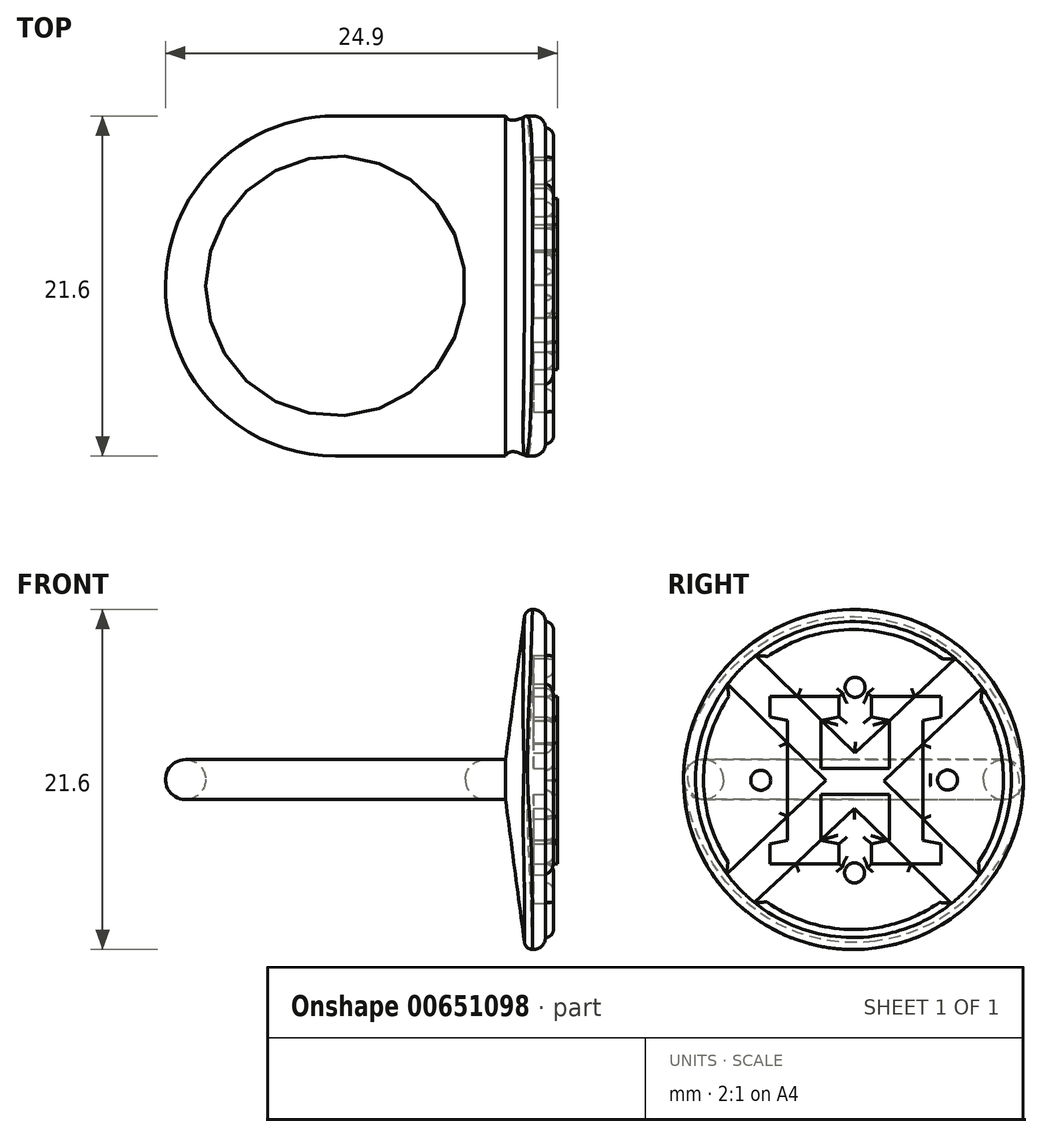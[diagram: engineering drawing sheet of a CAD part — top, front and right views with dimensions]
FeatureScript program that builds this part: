
annotation { "Feature Type Name" : "Feature", "Feature Type Description" : "" }
export const myFeature = defineFeature(function(context is Context, id is Id, definition is map)
    precondition{}
    {
        {
            var Q0;
            Q0=qCreatedBy(makeId("Top.planeOp"),FACE);
            var sketch = newSketch(context, id + "F0", { "sketchPlane" : qUnion([Q0])});
            skCircle(sketch, "E0", {"center": v(0, 0) * mm, "radius": 8.26 * mm});
            skCircle(sketch, "E1.0", {"center": v(0, 0) * mm, "radius": 10.8 * mm});
            skLineSegment(sketch, "E2", {"start": v(0, -10.8) * mm, "end": v(28.84, -10.8) * mm});
            skLineSegment(sketch, "E3", {"start": v(0, 10.8) * mm, "end": v(27.85, 10.8) * mm});
            skLineSegment(sketch, "E4", {"start": v(10.8, 0) * mm, "end": v(10.8, 10.8) * mm});
            skLineSegment(sketch, "E5", {"start": v(10.8, 10.8) * mm, "end": v(10.8, -10.8) * mm});
            skSolve(sketch);
        }
        {
            var Q0;
            Q0=qSketchRegion(id+"F0",true);
            extrude(context, id + "F1", {"entities" : qUnion([Q0]), "depth" : 2.54 * mm, "offsetDistance" : 25.4 * mm});
        }
        {
            var Q0;
            Q0=makeQuery(id+"F1.opExtrude","CAP_EDGE",EDGE,{"disambiguationData":[OSD([sQuery(id+"F0.wireOp",EDGE,"E0")])],"isStart":false});
            var Q1;
            Q1=makeQuery(id+"F1.opExtrude","CAP_EDGE",EDGE,{"disambiguationData":[OSD([sQuery(id+"F0.wireOp",EDGE,"E0")])],"isStart":true});
            var Q2;
            Q2=makeQuery(id+"F1.opExtrude","CAP_EDGE",EDGE,{"disambiguationData":[OSD([sQuery(id+"F0.wireOp",EDGE,"E1.0")])],"isStart":false});
            var Q3;
            Q3=makeQuery(id+"F1.opExtrude","CAP_EDGE",EDGE,{"disambiguationData":[OSD([sQuery(id+"F0.wireOp",EDGE,"E1.0")])],"isStart":true});
            fillet(context, id + "F2", {"entities" : qUnion([Q0, Q1, Q2, Q3]), "radius" : 1.27 * mm, "tangentPropagation" : true, "allowEdgeOverflow" : false});
        }
        {
            var Q0;
            Q0=makeQuery(id+"F1.opExtrude","SWEPT_FACE",FACE,{"disambiguationData":[OSD([sQuery(id+"F0.wireOp",EDGE,"E5")])]});
            cPlane(context, id + "F3", {"entities" : qUnion([Q0]), "cplaneType" : CPlaneType.OFFSET, "offset" : 1.27 * mm, "width" : 152.4 * mm, "height" : 152.4 * mm});
        }
        {
            var Q0;
            Q0=qCreatedBy(id+"F3.planeOp",FACE);
            var sketch = newSketch(context, id + "F4", { "sketchPlane" : qUnion([Q0])});
            skLineSegment(sketch, "E6", {"start": v(0, 0) * mm, "end": v(0, 2.54) * mm});
            skCircle(sketch, "E7", {"center": v(0, 1.27) * mm, "radius": 10.8 * mm});
            skSolve(sketch);
        }
        {
            var Q1;
            Q1=makeQuery(id+"F1.opExtrude","SWEPT_FACE",FACE,{"disambiguationData":[OSD([sQuery(id+"F0.wireOp",EDGE,"E5")])]});
            var Q2;
            Q2=makeQuery(id+"F4.imprint","IMPRINT",FACE,{"disambiguationData":[TD([[makeQuery(id+"F4.imprint","IMPRINT",EDGE,{"derivedFrom":sQuery(id+"F4.wireOp",EDGE,"E7")}),1.0]])]});
            loft(context, id + "F5", {"operationType" : NewBodyOperationType.ADD, "sheetProfilesArray" : [{ "sheetProfileEntities" : qUnion([Q1]) }, { "sheetProfileEntities" : qUnion([Q2]) }]});
        }
        {
            var Q0;
            Q0=makeQuery(id+"F5.opLoft","CAP_FACE",FACE,{"disambiguationData":[OSD([makeQuery(id+"F4.imprint","IMPRINT",FACE,{"disambiguationData":[TD([[makeQuery(id+"F4.imprint","IMPRINT",EDGE,{"derivedFrom":sQuery(id+"F4.wireOp",EDGE,"E7")}),1.0]])]})])],"isStart":true});
            extrude(context, id + "F6", {"entities" : qUnion([Q0]), "operationType" : NewBodyOperationType.ADD, "depth" : 1.27 * mm, "offsetDistance" : 25.4 * mm});
        }
        {
            var Q0;
            {var subQ0=sQuery(id+"F4.wireOp",EDGE,"E7");var subQ1=sQuery(id+"F0.wireOp",EDGE,"E5");var subQ2=makeQuery(id+"F1.opExtrude","SWEPT_FACE",FACE,{"disambiguationData":[OSD([subQ1])]});var subQ3=sQuery(id+"F0.wireOp",EDGE,"E3");var subQ4=sQuery(id+"F0.wireOp",EDGE,"E2");var subQ5=sQuery(id+"F0.wireOp",EDGE,"E1.0");var subQ6=sQuery(id+"F0.wireOp",EDGE,"E0");var subQ7=makeQuery(id+"F5.opLoft","MID_CAP_EDGE",EDGE,{"disambiguationData":[OSD([subQ6,subQ5,subQ4,subQ3,subQ1,subQ0]),TDD([makeQuery(id+"F2.opFillet","BLEND_VERTEX",VERTEX,{"blendedFrom":[makeQuery(id+"F1.opExtrude","CAP_EDGE",EDGE,{"disambiguationData":[OSD([subQ3])],"isStart":true}),makeQuery(id+"F1.opExtrude","CAP_FACE",FACE,{"disambiguationData":[OSD([subQ6,subQ5,subQ4,subQ3,subQ1])],"isStart":true}),subQ2],"blendedInto":[makeQuery(id+"F1.opExtrude","CAP_FACE",FACE,{"disambiguationData":[OSD([subQ6,subQ5,subQ4,subQ3,subQ1])],"isStart":true}),subQ2]}),makeQuery(id+"F2.opFillet","BLEND_VERTEX",VERTEX,{"blendedFrom":[makeQuery(id+"F1.opExtrude","CAP_EDGE",EDGE,{"disambiguationData":[OSD([subQ3])],"isStart":false}),makeQuery(id+"F1.opExtrude","CAP_FACE",FACE,{"disambiguationData":[OSD([subQ6,subQ5,subQ4,subQ3,subQ1])],"isStart":false}),subQ2],"blendedInto":[makeQuery(id+"F1.opExtrude","CAP_FACE",FACE,{"disambiguationData":[OSD([subQ6,subQ5,subQ4,subQ3,subQ1])],"isStart":false}),subQ2]}),makeQuery(id+"F4.imprint","IMPRINT",EDGE,{"derivedFrom":subQ0})])],"capPos":1.0});Q0=makeQuery(id+"F6.boolean.opBoolean","MERGE",EDGE,{"derivedFrom":[subQ7,makeQuery(id+"F6.opExtrude","CAP_EDGE",EDGE,{"disambiguationData":[OSD([subQ6,subQ5,subQ4,subQ3,subQ1,subQ0]),TDD([subQ7])],"isStart":true})]});}
            var Q1;
            {var subQ0=sQuery(id+"F4.wireOp",EDGE,"E7");var subQ1=sQuery(id+"F0.wireOp",EDGE,"E5");var subQ2=makeQuery(id+"F1.opExtrude","SWEPT_FACE",FACE,{"disambiguationData":[OSD([subQ1])]});var subQ3=sQuery(id+"F0.wireOp",EDGE,"E3");var subQ4=sQuery(id+"F0.wireOp",EDGE,"E2");var subQ5=sQuery(id+"F0.wireOp",EDGE,"E1.0");var subQ6=sQuery(id+"F0.wireOp",EDGE,"E0");var subQ7=makeQuery(id+"F1.opExtrude","CAP_FACE",FACE,{"disambiguationData":[OSD([subQ6,subQ5,subQ4,subQ3,subQ1])],"isStart":true});var subQ8=makeQuery(id+"F5.opLoft","MID_CAP_EDGE",EDGE,{"disambiguationData":[OSD([subQ6,subQ5,subQ4,subQ3,subQ1,subQ0]),TDD([makeQuery(id+"F2.opFillet","BLEND_VERTEX",VERTEX,{"blendedFrom":[makeQuery(id+"F1.opExtrude","CAP_EDGE",EDGE,{"disambiguationData":[OSD([subQ4])],"isStart":true}),subQ7,subQ2],"blendedInto":[subQ7,subQ2]}),makeQuery(id+"F2.opFillet","BLEND_VERTEX",VERTEX,{"blendedFrom":[makeQuery(id+"F1.opExtrude","CAP_EDGE",EDGE,{"disambiguationData":[OSD([subQ3])],"isStart":true}),subQ7,subQ2],"blendedInto":[subQ7,subQ2]}),makeQuery(id+"F4.imprint","IMPRINT",EDGE,{"derivedFrom":subQ0})])],"capPos":1.0});Q1=makeQuery(id+"F6.boolean.opBoolean","MERGE",EDGE,{"derivedFrom":[subQ8,makeQuery(id+"F6.opExtrude","CAP_EDGE",EDGE,{"disambiguationData":[OSD([subQ6,subQ5,subQ4,subQ3,subQ1,subQ0]),TDD([subQ8])],"isStart":true})]});}
            fillet(context, id + "F7", {"entities" : qUnion([Q0, Q1]), "radius" : 0.5 * mm, "tangentPropagation" : true, "allowEdgeOverflow" : false});
        }
        {
            var Q0;
            {var subQ0=sQuery(id+"F4.wireOp",EDGE,"E7");var subQ1=sQuery(id+"F0.wireOp",EDGE,"E5");var subQ2=makeQuery(id+"F1.opExtrude","SWEPT_FACE",FACE,{"disambiguationData":[OSD([subQ1])]});var subQ3=sQuery(id+"F0.wireOp",EDGE,"E3");var subQ4=sQuery(id+"F0.wireOp",EDGE,"E2");var subQ5=sQuery(id+"F0.wireOp",EDGE,"E1.0");var subQ6=sQuery(id+"F0.wireOp",EDGE,"E0");var subQ7=makeQuery(id+"F1.opExtrude","CAP_FACE",FACE,{"disambiguationData":[OSD([subQ6,subQ5,subQ4,subQ3,subQ1])],"isStart":true});Q0=makeQuery(id+"F6.opExtrude","CAP_EDGE",EDGE,{"disambiguationData":[OSD([subQ6,subQ5,subQ4,subQ3,subQ1,subQ0]),TDD([makeQuery(id+"F5.opLoft","MID_CAP_EDGE",EDGE,{"disambiguationData":[OSD([subQ6,subQ5,subQ4,subQ3,subQ1,subQ0]),TDD([makeQuery(id+"F2.opFillet","BLEND_VERTEX",VERTEX,{"blendedFrom":[makeQuery(id+"F1.opExtrude","CAP_EDGE",EDGE,{"disambiguationData":[OSD([subQ4])],"isStart":true}),subQ7,subQ2],"blendedInto":[subQ7,subQ2]}),makeQuery(id+"F2.opFillet","BLEND_VERTEX",VERTEX,{"blendedFrom":[makeQuery(id+"F1.opExtrude","CAP_EDGE",EDGE,{"disambiguationData":[OSD([subQ3])],"isStart":true}),subQ7,subQ2],"blendedInto":[subQ7,subQ2]}),makeQuery(id+"F4.imprint","IMPRINT",EDGE,{"derivedFrom":subQ0})])],"capPos":1.0})])],"isStart":false});}
            var Q1;
            {var subQ0=sQuery(id+"F4.wireOp",EDGE,"E7");var subQ1=sQuery(id+"F0.wireOp",EDGE,"E5");var subQ2=sQuery(id+"F0.wireOp",EDGE,"E3");var subQ3=sQuery(id+"F0.wireOp",EDGE,"E2");var subQ4=sQuery(id+"F0.wireOp",EDGE,"E1.0");var subQ5=sQuery(id+"F0.wireOp",EDGE,"E0");Q1=makeQuery(id+"F6.opExtrude","CAP_EDGE",EDGE,{"disambiguationData":[OSD([subQ5,subQ4,subQ3,subQ2,subQ1,subQ0]),TDD([makeQuery(id+"F5.opLoft","MID_CAP_EDGE",EDGE,{"disambiguationData":[OSD([subQ5,subQ4,subQ3,subQ2,subQ1,subQ0]),TDD([makeQuery(id+"F2.opFillet","BLEND_VERTEX",VERTEX,{"blendedFrom":[makeQuery(id+"F1.opExtrude","CAP_EDGE",EDGE,{"disambiguationData":[OSD([subQ3])],"isStart":true}),makeQuery(id+"F1.opExtrude","CAP_FACE",FACE,{"disambiguationData":[OSD([subQ5,subQ4,subQ3,subQ2,subQ1])],"isStart":true}),makeQuery(id+"F1.opExtrude","SWEPT_FACE",FACE,{"disambiguationData":[OSD([subQ1])]})],"blendedInto":[makeQuery(id+"F1.opExtrude","CAP_FACE",FACE,{"disambiguationData":[OSD([subQ5,subQ4,subQ3,subQ2,subQ1])],"isStart":true}),makeQuery(id+"F1.opExtrude","SWEPT_FACE",FACE,{"disambiguationData":[OSD([subQ1])]})]}),makeQuery(id+"F4.imprint","IMPRINT",EDGE,{"derivedFrom":subQ0})])],"capPos":1.0})])],"isStart":false});}
            fillet(context, id + "F8", {"entities" : qUnion([Q0, Q1]), "radius" : 0.76 * mm, "tangentPropagation" : true, "allowEdgeOverflow" : false});
        }
        {
            var Q0;
            Q0=makeQuery(id+"F6.opExtrude","CAP_FACE",FACE,{"disambiguationData":[OSD([makeQuery(id+"F4.imprint","IMPRINT",FACE,{"disambiguationData":[TD([[makeQuery(id+"F4.imprint","IMPRINT",EDGE,{"derivedFrom":sQuery(id+"F4.wireOp",EDGE,"E7")}),1.0]])]})])],"isStart":false});
            var sketch = newSketch(context, id + "F9", { "sketchPlane" : qUnion([Q0])});
            skLineSegment(sketch, "E8.0", {"start": v(-7.14, 6.5) * mm, "end": v(-1.75, 1.22) * mm});
            skLineSegment(sketch, "E9.0", {"start": v(-5.37, 8.31) * mm, "end": v(0.1, 2.96) * mm});
            skLineSegment(sketch, "E10.0", {"start": v(5.58, 8.12) * mm, "end": v(0.1, 2.96) * mm});
            skLineSegment(sketch, "E11.0", {"start": v(7.33, 6.27) * mm, "end": v(1.92, 1.18) * mm});
            skLineSegment(sketch, "E12.trimOffspring", {"start": v(-1.75, 1.22) * mm, "end": v(-7.17, -3.9) * mm});
            skLineSegment(sketch, "E13.trimOffspring", {"start": v(1.92, 1.18) * mm, "end": v(7.16, -3.95) * mm});
            skLineSegment(sketch, "E14.trimOffspring", {"start": v(0.07, -0.56) * mm, "end": v(-5.43, -5.74) * mm});
            skLineSegment(sketch, "E15.trimOffspring", {"start": v(0.07, -0.56) * mm, "end": v(5.38, -5.76) * mm});
            skLineSegment(sketch, "E16", {"start": v(7.16, -3.95) * mm, "end": v(8, -4.78) * mm});
            skLineSegment(sketch, "E17", {"start": v(8, -4.78) * mm, "end": v(1.92, 1.18) * mm});
            skLineSegment(sketch, "E18", {"start": v(6.23, -6.6) * mm, "end": v(5.38, -5.76) * mm});
            skLineSegment(sketch, "E19", {"start": v(-5.43, -5.74) * mm, "end": v(-6.29, -6.55) * mm});
            skLineSegment(sketch, "E20", {"start": v(-6.29, -6.55) * mm, "end": v(0.07, -0.56) * mm});
            skLineSegment(sketch, "E21", {"start": v(-7.17, -3.9) * mm, "end": v(-8.05, -4.72) * mm});
            skLineSegment(sketch, "E22", {"start": v(-8.05, -4.72) * mm, "end": v(-1.75, 1.22) * mm});
            skLineSegment(sketch, "E23.trimOffspring", {"start": v(0.1, 2.96) * mm, "end": v(6.46, 8.95) * mm});
            skLineSegment(sketch, "E24.trimOffspring", {"start": v(0.1, 2.96) * mm, "end": v(-6.22, 9.14) * mm});
            skLineSegment(sketch, "E25.trimOffspring", {"start": v(1.92, 1.18) * mm, "end": v(8.18, 7.08) * mm});
            skLineSegment(sketch, "E26.trimOffspring", {"start": v(-1.75, 1.22) * mm, "end": v(-8, 7.33) * mm});
            skLineSegment(sketch, "E27.trimOffspring", {"start": v(0.07, -0.56) * mm, "end": v(6.23, -6.6) * mm});
            skLineSegment(sketch, "E28", {"start": v(0.1, 2.96) * mm, "end": v(0.1, 11.3) * mm});
            skCircle(sketch, "E29", {"center": v(0.1, 7.13) * mm, "radius": 0.64 * mm});
            skLineSegment(sketch, "E30", {"start": v(1.92, 1.18) * mm, "end": v(10.03, 1.3) * mm});
            skPoint(sketch, "E30.endSnap0", {"position": v(4.75, 1.3) * mm});
            skCircle(sketch, "E31", {"center": v(5.98, 1.24) * mm, "radius": 0.64 * mm});
            skLineSegment(sketch, "E32", {"start": v(0.07, -0.56) * mm, "end": v(0.07, -8.76) * mm});
            skCircle(sketch, "E33", {"center": v(0.07, -4.66) * mm, "radius": 0.64 * mm});
            skLineSegment(sketch, "E34", {"start": v(-1.75, 1.22) * mm, "end": v(-10.03, 1.22) * mm});
            skCircle(sketch, "E35", {"center": v(-5.9, 1.22) * mm, "radius": 0.64 * mm});
            skText(sketch, "E36", { "text": "H", "fontName": "RobotoSlab-Bold.ttf"});
            const initialGuessF9  = {"E36": [-0.00572, -0.00408, 1, 0, 0.01075]};
            skSetInitialGuess(sketch, initialGuessF9);
            skSolve(sketch);
        }
        {
            var Q0;
            {var subQ0=sQuery(id+"F9.wireOp",EDGE,"E31");var subQ1=sQuery(id+"F9.wireOp",EDGE,"E30");var subQ2=makeQuery(id+"F9.imprint","INTERSECT",VERTEX,{"disambiguationData":[OD(0.0)],"derivedFrom":[subQ1,subQ0]});Q0=makeQuery(id+"F9.imprint","IMPRINT",FACE,{"disambiguationData":[TD([[makeQuery(id+"F9.imprint","IMPRINT",EDGE,{"disambiguationData":[TD([[subQ2,-1.0]])],"derivedFrom":subQ1}),1.0]])]});}
            var Q1;
            {var subQ0=sQuery(id+"F9.wireOp",EDGE,"E31");var subQ1=sQuery(id+"F9.wireOp",EDGE,"E30");var subQ2=makeQuery(id+"F9.imprint","INTERSECT",VERTEX,{"disambiguationData":[OD(0.0)],"derivedFrom":[subQ1,subQ0]});Q1=makeQuery(id+"F9.imprint","IMPRINT",FACE,{"disambiguationData":[TD([[makeQuery(id+"F9.imprint","IMPRINT",EDGE,{"disambiguationData":[TD([[subQ2,-1.0]])],"derivedFrom":subQ1}),-1.0]])]});}
            var Q2;
            {var subQ0=sQuery(id+"F9.wireOp",EDGE,"E33");var subQ1=sQuery(id+"F9.wireOp",EDGE,"E32");var subQ2=makeQuery(id+"F9.imprint","INTERSECT",VERTEX,{"disambiguationData":[OD(0.0)],"derivedFrom":[subQ1,subQ0]});Q2=makeQuery(id+"F9.imprint","IMPRINT",FACE,{"disambiguationData":[TD([[makeQuery(id+"F9.imprint","IMPRINT",EDGE,{"disambiguationData":[TD([[subQ2,-1.0]])],"derivedFrom":subQ1}),1.0]])]});}
            var Q3;
            {var subQ0=sQuery(id+"F9.wireOp",EDGE,"E33");var subQ1=sQuery(id+"F9.wireOp",EDGE,"E32");var subQ2=makeQuery(id+"F9.imprint","INTERSECT",VERTEX,{"disambiguationData":[OD(0.0)],"derivedFrom":[subQ1,subQ0]});Q3=makeQuery(id+"F9.imprint","IMPRINT",FACE,{"disambiguationData":[TD([[makeQuery(id+"F9.imprint","IMPRINT",EDGE,{"disambiguationData":[TD([[subQ2,-1.0]])],"derivedFrom":subQ1}),-1.0]])]});}
            var Q4;
            {var subQ0=sQuery(id+"F9.wireOp",EDGE,"E35");var subQ1=sQuery(id+"F9.wireOp",EDGE,"E34");var subQ2=makeQuery(id+"F9.imprint","INTERSECT",VERTEX,{"disambiguationData":[OD(0.0)],"derivedFrom":[subQ1,subQ0]});Q4=makeQuery(id+"F9.imprint","IMPRINT",FACE,{"disambiguationData":[TD([[makeQuery(id+"F9.imprint","IMPRINT",EDGE,{"disambiguationData":[TD([[subQ2,-1.0]])],"derivedFrom":subQ1}),-1.0]])]});}
            var Q5;
            {var subQ0=sQuery(id+"F9.wireOp",EDGE,"E35");var subQ1=sQuery(id+"F9.wireOp",EDGE,"E34");var subQ2=makeQuery(id+"F9.imprint","INTERSECT",VERTEX,{"disambiguationData":[OD(0.0)],"derivedFrom":[subQ1,subQ0]});Q5=makeQuery(id+"F9.imprint","IMPRINT",FACE,{"disambiguationData":[TD([[makeQuery(id+"F9.imprint","IMPRINT",EDGE,{"disambiguationData":[TD([[subQ2,-1.0]])],"derivedFrom":subQ1}),1.0]])]});}
            var Q6;
            {var subQ0=sQuery(id+"F9.wireOp",EDGE,"E29");var subQ1=sQuery(id+"F9.wireOp",EDGE,"E28");var subQ2=makeQuery(id+"F9.imprint","INTERSECT",VERTEX,{"disambiguationData":[OD(0.0)],"derivedFrom":[subQ1,subQ0]});Q6=makeQuery(id+"F9.imprint","IMPRINT",FACE,{"disambiguationData":[TD([[makeQuery(id+"F9.imprint","IMPRINT",EDGE,{"disambiguationData":[TD([[subQ2,-1.0]])],"derivedFrom":subQ1}),1.0]])]});}
            var Q7;
            {var subQ0=sQuery(id+"F9.wireOp",EDGE,"E29");var subQ1=sQuery(id+"F9.wireOp",EDGE,"E28");var subQ2=makeQuery(id+"F9.imprint","INTERSECT",VERTEX,{"disambiguationData":[OD(0.0)],"derivedFrom":[subQ1,subQ0]});Q7=makeQuery(id+"F9.imprint","IMPRINT",FACE,{"disambiguationData":[TD([[makeQuery(id+"F9.imprint","IMPRINT",EDGE,{"disambiguationData":[TD([[subQ2,-1.0]])],"derivedFrom":subQ1}),-1.0]])]});}
            extrude(context, id + "F10", {"entities" : qUnion([Q0, Q1, Q2, Q3, Q4, Q5, Q6, Q7]), "operationType" : NewBodyOperationType.ADD, "depth" : 0.5 * mm, "offsetDistance" : 25.4 * mm});
        }
        {
            var Q0;
            Q0=makeQuery(id+"F10.opExtrude","CAP_FACE",FACE,{"disambiguationData":[OSD([sQuery(id+"F9.wireOp",EDGE,"E29")])],"isStart":false});
            var Q1;
            Q1=makeQuery(id+"F10.opExtrude","CAP_FACE",FACE,{"disambiguationData":[OSD([sQuery(id+"F9.wireOp",EDGE,"E31")])],"isStart":false});
            var Q2;
            Q2=makeQuery(id+"F10.opExtrude","CAP_FACE",FACE,{"disambiguationData":[OSD([sQuery(id+"F9.wireOp",EDGE,"E33")])],"isStart":false});
            var Q3;
            Q3=makeQuery(id+"F10.opExtrude","CAP_FACE",FACE,{"disambiguationData":[OSD([sQuery(id+"F9.wireOp",EDGE,"E35")])],"isStart":false});
            fillet(context, id + "F11", {"entities" : qUnion([Q0, Q1, Q2, Q3]), "radius" : 0.5 * mm, "tangentPropagation" : true, "allowEdgeOverflow" : false});
        }
        {
            var Q0;
            {var subQ20=sQuery(id+"F9.wireOp",EDGE,"E36.sketch_text.stroke-0");Q0=makeQuery(id+"F9.imprint","IMPRINT",FACE,{"disambiguationData":[TD([[makeQuery(id+"F9.imprint","IMPRINT",EDGE,{"derivedFrom":subQ20}),1.0]])]});}
            var Q1;
            {var subQ0=sQuery(id+"F9.wireOp",EDGE,"E36.sketch_text.stroke-4");Q1=makeQuery(id+"F9.imprint","IMPRINT",FACE,{"disambiguationData":[TD([[makeQuery(id+"F9.imprint","IMPRINT",EDGE,{"derivedFrom":subQ0}),1.0]])]});}
            var Q2;
            {var subQ0=sQuery(id+"F9.wireOp",EDGE,"E36.sketch_text.stroke-21");Q2=makeQuery(id+"F9.imprint","IMPRINT",FACE,{"disambiguationData":[TD([[makeQuery(id+"F9.imprint","IMPRINT",EDGE,{"derivedFrom":subQ0}),1.0]])]});}
            var Q3;
            {var subQ5=sQuery(id+"F9.wireOp",EDGE,"E22");Q3=makeQuery(id+"F9.imprint","IMPRINT",FACE,{"disambiguationData":[TD([[makeQuery(id+"F9.imprint","IMPRINT",EDGE,{"derivedFrom":subQ5}),-1.0]])]});}
            var Q4;
            {var subQ0=sQuery(id+"F9.wireOp",EDGE,"E36.sketch_text.stroke-15");Q4=makeQuery(id+"F9.imprint","IMPRINT",FACE,{"disambiguationData":[TD([[makeQuery(id+"F9.imprint","IMPRINT",EDGE,{"derivedFrom":subQ0}),1.0]])]});}
            var Q5;
            {var subQ20=sQuery(id+"F9.wireOp",EDGE,"E36.sketch_text.stroke-11");Q5=makeQuery(id+"F9.imprint","IMPRINT",FACE,{"disambiguationData":[TD([[makeQuery(id+"F9.imprint","IMPRINT",EDGE,{"derivedFrom":subQ20}),1.0]])]});}
            extrude(context, id + "F12", {"entities" : qUnion([Q0, Q1, Q2, Q3, Q4, Q5]), "operationType" : NewBodyOperationType.REMOVE, "oppositeDirection" : true, "depth" : 0.76 * mm, "offsetDistance" : 25.4 * mm});
        }
        {
            var Q0;
            {var subQ37=sQuery(id+"F9.wireOp",EDGE,"E36.sketch_text.stroke-0");Q0=makeQuery(id+"F9.imprint","IMPRINT",FACE,{"disambiguationData":[TD([[makeQuery(id+"F9.imprint","IMPRINT",EDGE,{"derivedFrom":subQ37}),-1.0]])]});}
            extrude(context, id + "F13", {"entities" : qUnion([Q0]), "operationType" : NewBodyOperationType.ADD, "depth" : 0.76 * mm, "offsetDistance" : 25.4 * mm});
        }
    });
